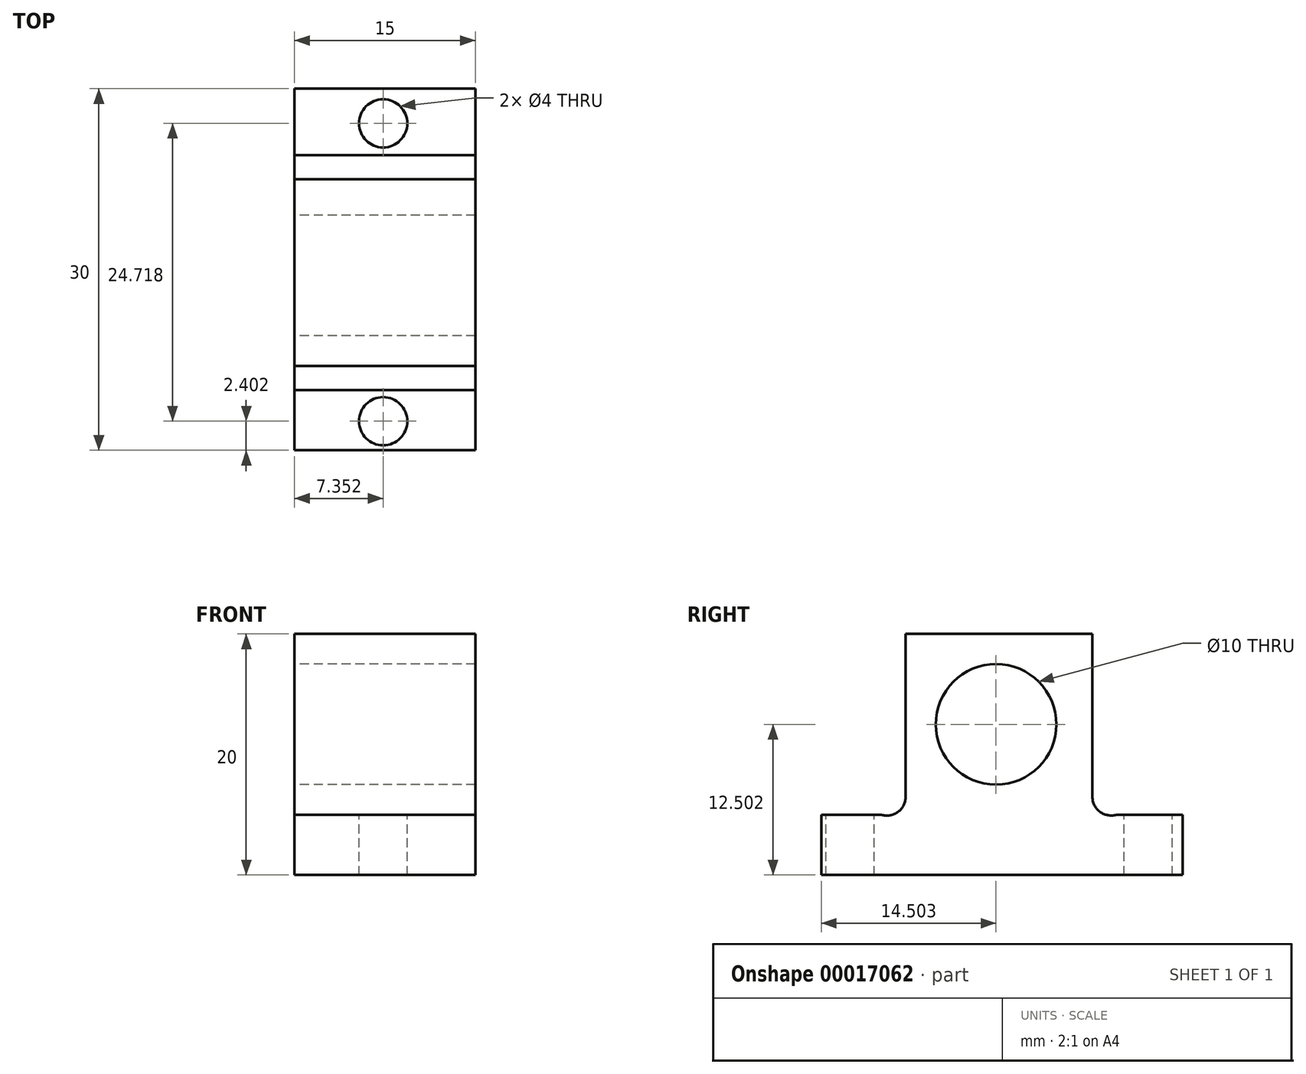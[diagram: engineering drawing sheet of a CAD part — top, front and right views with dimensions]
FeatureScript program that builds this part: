
annotation { "Feature Type Name" : "Feature", "Feature Type Description" : "" }
export const myFeature = defineFeature(function(context is Context, id is Id, definition is map)
    precondition{}
    {
        {
            var Q0;
            Q0=qCreatedBy(makeId("Right.planeOp"),FACE);
            var sketch = newSketch(context, id + "F0", { "sketchPlane" : qUnion([Q0])});
            skLineSegment(sketch, "E0", {"start": v(-23.15, 10.6) * mm, "end": v(-23.15, -2.9) * mm});
            skLineSegment(sketch, "E1", {"start": v(-23.15, 10.6) * mm, "end": v(-7.65, 10.6) * mm});
            skLineSegment(sketch, "E2", {"start": v(-7.65, 10.6) * mm, "end": v(-7.65, -2.9) * mm});
            skArc(sketch, "E3", {"start": v(-25.15, -4.4) * mm, "mid": v(-23.78, -4.16) * mm, "end": v(-23.15, -2.9) * mm});
            skLineSegment(sketch, "E4", {"start": v(-25.15, -4.4) * mm, "end": v(-30.15, -4.4) * mm});
            skLineSegment(sketch, "E5", {"start": v(-30.15, -4.4) * mm, "end": v(-30.15, -9.4) * mm});
            skLineSegment(sketch, "E6", {"start": v(-30.15, -9.4) * mm, "end": v(-0.15, -9.4) * mm});
            skLineSegment(sketch, "E7", {"start": v(-0.15, -9.4) * mm, "end": v(-0.15, -4.4) * mm});
            skCircle(sketch, "E8", {"center": v(-15.65, 3.1) * mm, "radius": 5 * mm});
            skArc(sketch, "E9", {"start": v(-7.65, -2.9) * mm, "mid": v(-7.03, -4.15) * mm, "end": v(-5.67, -4.4) * mm});
            skLineSegment(sketch, "E10", {"start": v(-5.67, -4.4) * mm, "end": v(-0.15, -4.4) * mm});
            skSolve(sketch);
        }
        {
            var Q0;
            Q0 = qSketchRegion(id + "F0", true);
            extrude(context, id + "F1", {"entities" : qUnion([Q0]), "depth" : 15 * mm});
        }
        {
            var Q0;
            Q0=makeQuery(id+"F1.opExtrude","SWEPT_FACE",FACE,{"disambiguationData":[OSD([sQuery(id+"F0.wireOp",EDGE,"E10")])]});
            var sketch = newSketch(context, id + "F2", { "sketchPlane" : qUnion([Q0])});
            skCircle(sketch, "E11", {"center": v(7.35, -3.03) * mm, "radius": 2 * mm});
            skCircle(sketch, "E12", {"center": v(7.35, -27.75) * mm, "radius": 2 * mm});
            skSolve(sketch);
        }
        {
            var Q0;
            Q0 = qSketchRegion(id + "F2", true);
            extrude(context, id + "F3", {"entities" : qUnion([Q0]), "operationType" : NewBodyOperationType.REMOVE, "endBound" : BoundingType.THROUGH_ALL, "oppositeDirection" : true, "depth" : 25 * mm});
        }
    });
